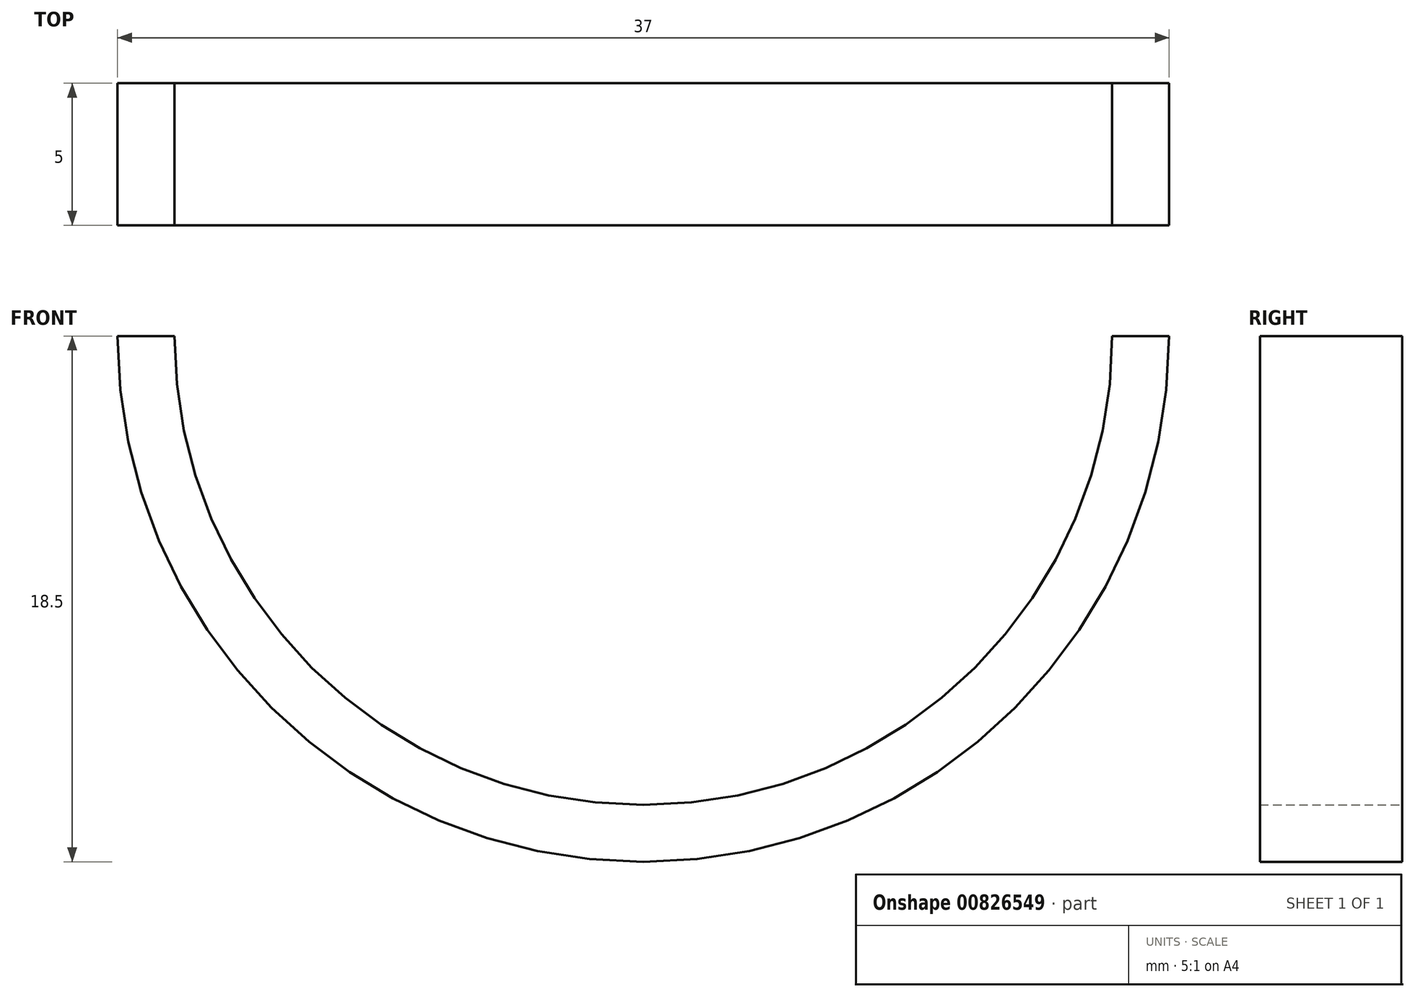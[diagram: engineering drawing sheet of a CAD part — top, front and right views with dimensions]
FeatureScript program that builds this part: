
annotation { "Feature Type Name" : "Feature", "Feature Type Description" : "" }
export const myFeature = defineFeature(function(context is Context, id is Id, definition is map)
    precondition{}
    {
        {
            var Q0;
            Q0=qCreatedBy(makeId("Front.planeOp"),FACE);
            var sketch = newSketch(context, id + "F0", { "sketchPlane" : qUnion([Q0])});
            skArc(sketch, "E0", {"start": v(-16.5, 0) * mm, "mid": v(0, -16.5) * mm, "end": v(16.5, 0) * mm});
            skArc(sketch, "E1.0", {"start": v(-18.5, 0) * mm, "mid": v(0, -18.5) * mm, "end": v(18.5, 0) * mm});
            skLineSegment(sketch, "E2", {"start": v(-16.5, 0) * mm, "end": v(-18.5, 0) * mm});
            skLineSegment(sketch, "E3", {"start": v(18.5, 0) * mm, "end": v(16.5, 0) * mm});
            skSolve(sketch);
        }
        {
            var Q0;
            Q0=makeQuery(id+"F0.imprint","IMPRINT",FACE,{"disambiguationData":[TD([[makeQuery(id+"F0.imprint","IMPRINT",EDGE,{"derivedFrom":sQuery(id+"F0.wireOp",EDGE,"E0")}),1.0]])]});
            var Q1;
            Q1=makeQuery(id+"F0.imprint","IMPRINT",FACE,{"disambiguationData":[TD([[makeQuery(id+"F0.imprint","IMPRINT",EDGE,{"derivedFrom":sQuery(id+"F0.wireOp",EDGE,"E0")}),-1.0]])]});
            extrude(context, id + "F1", {"entities" : qUnion([Q0, Q1]), "depth" : 5 * mm, "offsetDistance" : 25 * mm});
        }
    });
